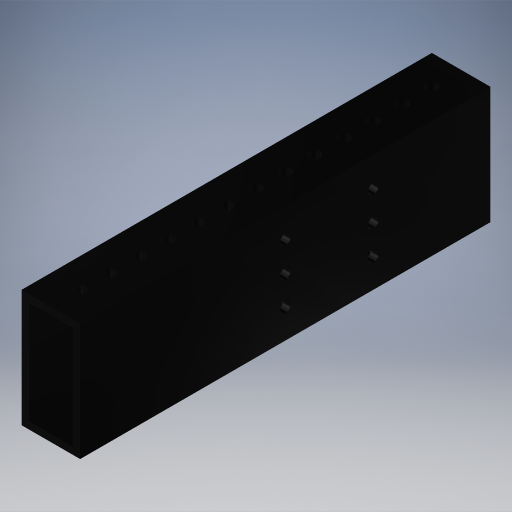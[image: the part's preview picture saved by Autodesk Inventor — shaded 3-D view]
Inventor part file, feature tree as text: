
AUTODESK INVENTOR PART (.ipt)
format: ipt  version: 2024.2 (Build 282272000, 272)  size: 753,664 bytes
history: native  units: in
note: dims shown in document units (in); Inventor stores cm internally (conversion verified against a paired STEP export)
features: other x13, extrude x10, hole x3, pattern_linear x3, mirror x3, sketch x2, sheet_metal_op x1, plane x1
ambient origin geometry x8: Origin, YZ Plane, XZ Plane, XY Plane, X Axis, Y Axis, Z Axis, Center Point
bodies: Solid1 (feature_tree)
feature tree (36):
  other  "Blocks"
  other  "Base Sketch"
  extrude  "Base"  Depth=1.0in
  extrude  "MAX Corner"  Depth=0.125in
  extrude  "MAX Corner Cut"  Depth=3.5in
  extrude  "Scribe Lines"  Depth=3.5in
  other  "Side Middle"
  other  "Top Middle"
  other  "Side Holes Sketch"
  hole  "Top Side Hole"  [1 undecoded]
  hole  "Mid Side Hole"  [1 undecoded]
  hole  "Btm Side Hole"  [1 undecoded]
  pattern_linear  "Side Holes"  Spacing1=7.0in  [1 undecoded]
  mirror  "Side Mirror"
  extrude  "MAXTube Hole"  TaperAngle=0.0deg  [1 undecoded]
  extrude  "MAXTube Outside"  Depth=7.0in
  pattern_linear  "MAXTube Pattern"  Spacing1=0.0in  [1 undecoded]
  mirror  "MAXTube Mirror"
  extrude  "Left Top Hole"  TaperAngle=0.0deg  [1 undecoded]
  extrude  "Mid Top Hole"  Depth=3.5in
  extrude  "Right Top Hole"  TaperAngle=0.0deg  [1 undecoded]
  pattern_linear  "Top Holes"  Spacing1=0.5in  [1 undecoded]
  mirror  "Top Mirror"
  extrude  "Extrusion14"  Depth=0.5in
  sketch  "Sketch9"  dims[d2=0.125in d3=0.125in d4=0.4375in d5=0.04in d6=0.0671in d7=0.0272in d8=0.0in d9=0.0in d10=0.0in d11=0.085in d12=0.085in d16=0.04in d17=0.04in d18=0.04in d19=0.04in d20=7.0in d21=0.0in d22=7.0in d23=0.0in d24=0.0in d25=0.0in d26=0.005in d30=0.0in d31=0.0in d34=0.5in d35=0.5in d38=0.5in d40=0.196in d41=0.75in d42=0.375in d43=0.25in d44=0.5635in d45=1.0in d46=0.8108in d47=0.196in d48=0.75in d49=0.375in d50=0.25in d51=0.5635in d52=1.0in d53=0.8108in d54=0.196in d55=0.75in d56=0.375in d57=0.25in d58=0.5635in d59=1.0in d60=0.8108in d61=0.5in d62=0.3937in d64=0.5in d69=1.5in d70=0.0in d71=0.0in d72=0.7874in d74=2.0in d78=2.0in d79=-3.5in d80=0.196in d81=0.0in d82=0.0in d83=0.5in d84=0.0in d85=0.0in d86=0.0in d87=0.0in d88=0.0in d89=0.0in d90=2.7559in d92=0.5in d93=1.0in d95=0.0in d96=0.0in d97=1.5in d98=4.0in d100=-3.5in d187=1.375in d188=0.0in d193=0.7874in d195=0.5in d196=0.7874in d198=0.5in d209=0.196in d210=0.5in d212=0.5in d213=3.5in d214=1.5in]
  sheet_metal_op  "Corner"
  other  "MAXTube"
  plane  "Work Plane3"
  sketch  "Sketch7"  dims[d0=2.0in d1=1.0in]
  other  "Corner:5"
  other  "Corner:6"
  other  "Corner:7"
  other  "Corner:8"
  other  "MAXTube:1"
  other  "MAXTube:2"
  other  "MAXTube:3"
note: 9 required parameter values undecoded (feature->parameter linkage not recoverable at this tier; creation-order binding heuristic only, values carry confidence <= 0.55)
